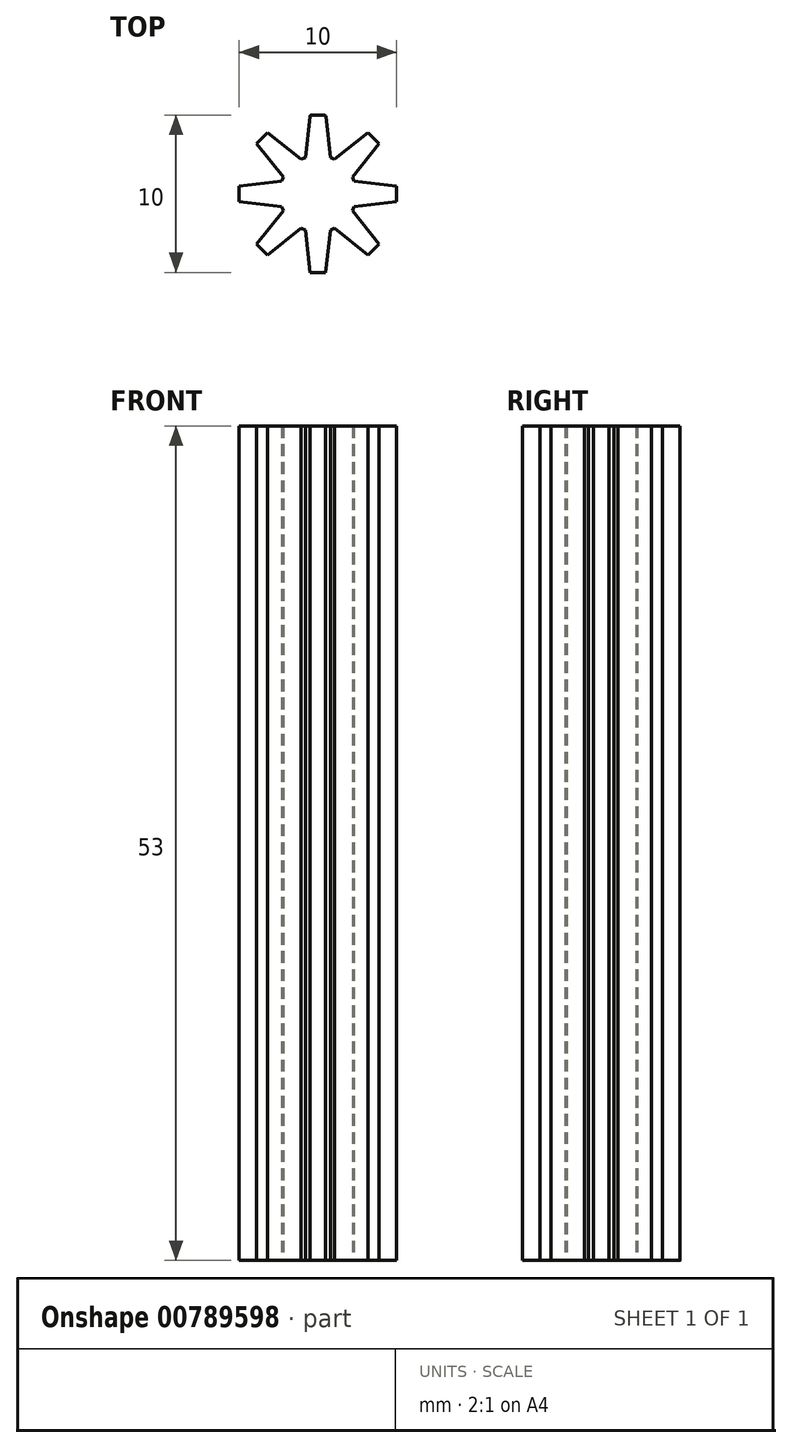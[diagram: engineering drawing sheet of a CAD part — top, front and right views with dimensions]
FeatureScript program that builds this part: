
annotation { "Feature Type Name" : "Feature", "Feature Type Description" : "" }
export const myFeature = defineFeature(function(context is Context, id is Id, definition is map)
    precondition{}
    {
        {
            var Q0;
            Q0=qCreatedBy(makeId("Top.planeOp"),FACE);
            var sketch = newSketch(context, id + "F0", { "sketchPlane" : qUnion([Q0])});
            skLineSegment(sketch, "E0", {"start": v(0, 5) * mm, "end": v(0.5, 5) * mm});
            skLineSegment(sketch, "E1", {"start": v(0.5, 5) * mm, "end": v(0.8, 2.3) * mm});
            skLineSegment(sketch, "E2.MirrorCS", {"start": v(-0.5, 5) * mm, "end": v(-0.8, 2.3) * mm});
            skLineSegment(sketch, "E3.MirrorCS", {"start": v(0, 5) * mm, "end": v(-0.5, 5) * mm});
            skLineSegment(sketch, "E4.1.0", {"start": v(-3.18, 3.89) * mm, "end": v(-1.06, 2.2) * mm});
            skLineSegment(sketch, "E4.1.1", {"start": v(-3.89, 3.18) * mm, "end": v(-2.2, 1.06) * mm});
            skLineSegment(sketch, "E4.1.2", {"start": v(-3.54, 3.54) * mm, "end": v(-3.89, 3.18) * mm});
            skLineSegment(sketch, "E4.1.3", {"start": v(-3.54, 3.54) * mm, "end": v(-3.18, 3.89) * mm});
            skLineSegment(sketch, "E4.1.4", {"start": v(-3.18, 3.89) * mm, "end": v(-1.06, 2.2) * mm});
            skLineSegment(sketch, "E4.1.5", {"start": v(-3.89, 3.18) * mm, "end": v(-2.2, 1.06) * mm});
            skLineSegment(sketch, "E4.1.6", {"start": v(-3.54, 3.54) * mm, "end": v(-3.18, 3.89) * mm});
            skLineSegment(sketch, "E4.1.7", {"start": v(-3.54, 3.54) * mm, "end": v(-3.89, 3.18) * mm});
            skLineSegment(sketch, "E4.1.8", {"start": v(-3.54, 3.54) * mm, "end": v(-3.89, 3.18) * mm});
            skLineSegment(sketch, "E4.1.9", {"start": v(-3.89, 3.18) * mm, "end": v(-2.2, 1.06) * mm});
            skLineSegment(sketch, "E4.1.10", {"start": v(-3.54, 3.54) * mm, "end": v(-3.18, 3.89) * mm});
            skLineSegment(sketch, "E4.1.11", {"start": v(-3.18, 3.89) * mm, "end": v(-1.06, 2.2) * mm});
            skLineSegment(sketch, "E4.1.12", {"start": v(-3.54, 3.54) * mm, "end": v(-3.89, 3.18) * mm});
            skLineSegment(sketch, "E4.1.13", {"start": v(-3.54, 3.54) * mm, "end": v(-3.18, 3.89) * mm});
            skLineSegment(sketch, "E4.2.0", {"start": v(-5, 0.5) * mm, "end": v(-2.3, 0.8) * mm});
            skLineSegment(sketch, "E4.2.1", {"start": v(-5, -0.5) * mm, "end": v(-2.3, -0.8) * mm});
            skLineSegment(sketch, "E4.2.2", {"start": v(-5, 0) * mm, "end": v(-5, -0.5) * mm});
            skLineSegment(sketch, "E4.2.3", {"start": v(-5, 0) * mm, "end": v(-5, 0.5) * mm});
            skLineSegment(sketch, "E4.2.4", {"start": v(-5, 0.5) * mm, "end": v(-2.3, 0.8) * mm});
            skLineSegment(sketch, "E4.2.5", {"start": v(-5, -0.5) * mm, "end": v(-2.3, -0.8) * mm});
            skLineSegment(sketch, "E4.2.6", {"start": v(-5, 0) * mm, "end": v(-5, 0.5) * mm});
            skLineSegment(sketch, "E4.2.7", {"start": v(-5, 0) * mm, "end": v(-5, -0.5) * mm});
            skLineSegment(sketch, "E4.2.8", {"start": v(-5, 0) * mm, "end": v(-5, -0.5) * mm});
            skLineSegment(sketch, "E4.2.9", {"start": v(-5, -0.5) * mm, "end": v(-2.3, -0.8) * mm});
            skLineSegment(sketch, "E4.2.10", {"start": v(-5, 0) * mm, "end": v(-5, 0.5) * mm});
            skLineSegment(sketch, "E4.2.11", {"start": v(-5, 0.5) * mm, "end": v(-2.3, 0.8) * mm});
            skLineSegment(sketch, "E4.2.12", {"start": v(-5, 0) * mm, "end": v(-5, -0.5) * mm});
            skLineSegment(sketch, "E4.2.13", {"start": v(-5, 0) * mm, "end": v(-5, 0.5) * mm});
            skLineSegment(sketch, "E4.3.0", {"start": v(-3.89, -3.18) * mm, "end": v(-2.2, -1.06) * mm});
            skLineSegment(sketch, "E4.3.1", {"start": v(-3.18, -3.89) * mm, "end": v(-1.06, -2.2) * mm});
            skLineSegment(sketch, "E4.3.2", {"start": v(-3.54, -3.54) * mm, "end": v(-3.18, -3.89) * mm});
            skLineSegment(sketch, "E4.3.3", {"start": v(-3.54, -3.54) * mm, "end": v(-3.89, -3.18) * mm});
            skLineSegment(sketch, "E4.3.4", {"start": v(-3.89, -3.18) * mm, "end": v(-2.2, -1.06) * mm});
            skLineSegment(sketch, "E4.3.5", {"start": v(-3.18, -3.89) * mm, "end": v(-1.06, -2.2) * mm});
            skLineSegment(sketch, "E4.3.6", {"start": v(-3.54, -3.54) * mm, "end": v(-3.89, -3.18) * mm});
            skLineSegment(sketch, "E4.3.7", {"start": v(-3.54, -3.54) * mm, "end": v(-3.18, -3.89) * mm});
            skLineSegment(sketch, "E4.3.8", {"start": v(-3.54, -3.54) * mm, "end": v(-3.18, -3.89) * mm});
            skLineSegment(sketch, "E4.3.9", {"start": v(-3.18, -3.89) * mm, "end": v(-1.06, -2.2) * mm});
            skLineSegment(sketch, "E4.3.10", {"start": v(-3.54, -3.54) * mm, "end": v(-3.89, -3.18) * mm});
            skLineSegment(sketch, "E4.3.11", {"start": v(-3.89, -3.18) * mm, "end": v(-2.2, -1.06) * mm});
            skLineSegment(sketch, "E4.3.12", {"start": v(-3.54, -3.54) * mm, "end": v(-3.18, -3.89) * mm});
            skLineSegment(sketch, "E4.3.13", {"start": v(-3.54, -3.54) * mm, "end": v(-3.89, -3.18) * mm});
            skLineSegment(sketch, "E4.4.0", {"start": v(-0.5, -5) * mm, "end": v(-0.8, -2.3) * mm});
            skLineSegment(sketch, "E4.4.1", {"start": v(0.5, -5) * mm, "end": v(0.8, -2.3) * mm});
            skLineSegment(sketch, "E4.4.2", {"start": v(0, -5) * mm, "end": v(0.5, -5) * mm});
            skLineSegment(sketch, "E4.4.3", {"start": v(0, -5) * mm, "end": v(-0.5, -5) * mm});
            skLineSegment(sketch, "E4.4.4", {"start": v(-0.5, -5) * mm, "end": v(-0.8, -2.3) * mm});
            skLineSegment(sketch, "E4.4.5", {"start": v(0.5, -5) * mm, "end": v(0.8, -2.3) * mm});
            skLineSegment(sketch, "E4.4.6", {"start": v(0, -5) * mm, "end": v(-0.5, -5) * mm});
            skLineSegment(sketch, "E4.4.7", {"start": v(0, -5) * mm, "end": v(0.5, -5) * mm});
            skLineSegment(sketch, "E4.4.8", {"start": v(0, -5) * mm, "end": v(0.5, -5) * mm});
            skLineSegment(sketch, "E4.4.9", {"start": v(0.5, -5) * mm, "end": v(0.8, -2.3) * mm});
            skLineSegment(sketch, "E4.4.10", {"start": v(0, -5) * mm, "end": v(-0.5, -5) * mm});
            skLineSegment(sketch, "E4.4.11", {"start": v(-0.5, -5) * mm, "end": v(-0.8, -2.3) * mm});
            skLineSegment(sketch, "E4.4.12", {"start": v(0, -5) * mm, "end": v(0.5, -5) * mm});
            skLineSegment(sketch, "E4.4.13", {"start": v(0, -5) * mm, "end": v(-0.5, -5) * mm});
            skLineSegment(sketch, "E4.5.0", {"start": v(3.18, -3.89) * mm, "end": v(1.06, -2.2) * mm});
            skLineSegment(sketch, "E4.5.1", {"start": v(3.89, -3.18) * mm, "end": v(2.2, -1.06) * mm});
            skLineSegment(sketch, "E4.5.2", {"start": v(3.54, -3.54) * mm, "end": v(3.89, -3.18) * mm});
            skLineSegment(sketch, "E4.5.3", {"start": v(3.54, -3.54) * mm, "end": v(3.18, -3.89) * mm});
            skLineSegment(sketch, "E4.5.4", {"start": v(3.18, -3.89) * mm, "end": v(1.06, -2.2) * mm});
            skLineSegment(sketch, "E4.5.5", {"start": v(3.89, -3.18) * mm, "end": v(2.2, -1.06) * mm});
            skLineSegment(sketch, "E4.5.6", {"start": v(3.54, -3.54) * mm, "end": v(3.18, -3.89) * mm});
            skLineSegment(sketch, "E4.5.7", {"start": v(3.54, -3.54) * mm, "end": v(3.89, -3.18) * mm});
            skLineSegment(sketch, "E4.5.8", {"start": v(3.54, -3.54) * mm, "end": v(3.89, -3.18) * mm});
            skLineSegment(sketch, "E4.5.9", {"start": v(3.89, -3.18) * mm, "end": v(2.2, -1.06) * mm});
            skLineSegment(sketch, "E4.5.10", {"start": v(3.54, -3.54) * mm, "end": v(3.18, -3.89) * mm});
            skLineSegment(sketch, "E4.5.11", {"start": v(3.18, -3.89) * mm, "end": v(1.06, -2.2) * mm});
            skLineSegment(sketch, "E4.5.12", {"start": v(3.54, -3.54) * mm, "end": v(3.89, -3.18) * mm});
            skLineSegment(sketch, "E4.5.13", {"start": v(3.54, -3.54) * mm, "end": v(3.18, -3.89) * mm});
            skLineSegment(sketch, "E4.6.0", {"start": v(5, -0.5) * mm, "end": v(2.3, -0.8) * mm});
            skLineSegment(sketch, "E4.6.1", {"start": v(5, 0.5) * mm, "end": v(2.3, 0.8) * mm});
            skLineSegment(sketch, "E4.6.2", {"start": v(5, 0) * mm, "end": v(5, 0.5) * mm});
            skLineSegment(sketch, "E4.6.3", {"start": v(5, 0) * mm, "end": v(5, -0.5) * mm});
            skLineSegment(sketch, "E4.6.4", {"start": v(5, -0.5) * mm, "end": v(2.3, -0.8) * mm});
            skLineSegment(sketch, "E4.6.5", {"start": v(5, 0.5) * mm, "end": v(2.3, 0.8) * mm});
            skLineSegment(sketch, "E4.6.6", {"start": v(5, 0) * mm, "end": v(5, -0.5) * mm});
            skLineSegment(sketch, "E4.6.7", {"start": v(5, 0) * mm, "end": v(5, 0.5) * mm});
            skLineSegment(sketch, "E4.6.8", {"start": v(5, 0) * mm, "end": v(5, 0.5) * mm});
            skLineSegment(sketch, "E4.6.9", {"start": v(5, 0.5) * mm, "end": v(2.3, 0.8) * mm});
            skLineSegment(sketch, "E4.6.10", {"start": v(5, 0) * mm, "end": v(5, -0.5) * mm});
            skLineSegment(sketch, "E4.6.11", {"start": v(5, -0.5) * mm, "end": v(2.3, -0.8) * mm});
            skLineSegment(sketch, "E4.6.12", {"start": v(5, 0) * mm, "end": v(5, 0.5) * mm});
            skLineSegment(sketch, "E4.6.13", {"start": v(5, 0) * mm, "end": v(5, -0.5) * mm});
            skLineSegment(sketch, "E4.7.0", {"start": v(3.89, 3.18) * mm, "end": v(2.2, 1.06) * mm});
            skLineSegment(sketch, "E4.7.1", {"start": v(3.18, 3.89) * mm, "end": v(1.06, 2.2) * mm});
            skLineSegment(sketch, "E4.7.2", {"start": v(3.54, 3.54) * mm, "end": v(3.18, 3.89) * mm});
            skLineSegment(sketch, "E4.7.3", {"start": v(3.54, 3.54) * mm, "end": v(3.89, 3.18) * mm});
            skLineSegment(sketch, "E4.7.4", {"start": v(3.89, 3.18) * mm, "end": v(2.2, 1.06) * mm});
            skLineSegment(sketch, "E4.7.5", {"start": v(3.18, 3.89) * mm, "end": v(1.06, 2.2) * mm});
            skLineSegment(sketch, "E4.7.6", {"start": v(3.54, 3.54) * mm, "end": v(3.89, 3.18) * mm});
            skLineSegment(sketch, "E4.7.7", {"start": v(3.54, 3.54) * mm, "end": v(3.18, 3.89) * mm});
            skLineSegment(sketch, "E4.7.8", {"start": v(3.54, 3.54) * mm, "end": v(3.18, 3.89) * mm});
            skLineSegment(sketch, "E4.7.9", {"start": v(3.18, 3.89) * mm, "end": v(1.06, 2.2) * mm});
            skLineSegment(sketch, "E4.7.10", {"start": v(3.54, 3.54) * mm, "end": v(3.89, 3.18) * mm});
            skLineSegment(sketch, "E4.7.11", {"start": v(3.89, 3.18) * mm, "end": v(2.2, 1.06) * mm});
            skLineSegment(sketch, "E4.7.12", {"start": v(3.54, 3.54) * mm, "end": v(3.18, 3.89) * mm});
            skLineSegment(sketch, "E4.7.13", {"start": v(3.54, 3.54) * mm, "end": v(3.89, 3.18) * mm});
            skPoint(sketch, "E4.center", {"position": v(0, 0) * mm});
            skLineSegment(sketch, "E5", {"start": v(-2.2, 1.06) * mm, "end": v(-2.3, 0.8) * mm});
            skLineSegment(sketch, "E6", {"start": v(-2.3, -0.8) * mm, "end": v(-2.2, -1.06) * mm});
            skLineSegment(sketch, "E7", {"start": v(-1.06, -2.2) * mm, "end": v(-0.8, -2.3) * mm});
            skLineSegment(sketch, "E8", {"start": v(0.8, -2.3) * mm, "end": v(1.06, -2.2) * mm});
            skLineSegment(sketch, "E9", {"start": v(2.2, -1.06) * mm, "end": v(2.3, -0.8) * mm});
            skLineSegment(sketch, "E10", {"start": v(2.3, 0.8) * mm, "end": v(2.2, 1.06) * mm});
            skLineSegment(sketch, "E11", {"start": v(1.06, 2.2) * mm, "end": v(0.8, 2.3) * mm});
            skLineSegment(sketch, "E12", {"start": v(-0.8, 2.3) * mm, "end": v(-1.06, 2.2) * mm});
            skSolve(sketch);
        }
        {
            var Q0;
            Q0 = qSketchRegion(id + "F0", true);
            extrude(context, id + "F1", {"entities" : qUnion([Q0]), "depth" : 53 * mm, "offsetDistance" : 25 * mm});
        }
        {
            var Q0;
            Q0=makeQuery(id+"F1.opExtrude","SWEPT_EDGE",EDGE,{"disambiguationData":[OSD([sQuery(id+"F0.wireOp",EDGE,"E4.7.11"),sQuery(id+"F0.wireOp",EDGE,"E4.7.13")])]});
            var Q1;
            Q1=makeQuery(id+"F1.opExtrude","SWEPT_EDGE",EDGE,{"disambiguationData":[OSD([sQuery(id+"F0.wireOp",EDGE,"E4.7.9"),sQuery(id+"F0.wireOp",EDGE,"E4.7.12")])]});
            var Q2;
            Q2=makeQuery(id+"F1.opExtrude","SWEPT_EDGE",EDGE,{"disambiguationData":[OSD([sQuery(id+"F0.wireOp",EDGE,"E4.6.9"),sQuery(id+"F0.wireOp",EDGE,"E4.6.12")])]});
            var Q3;
            Q3=makeQuery(id+"F1.opExtrude","SWEPT_EDGE",EDGE,{"disambiguationData":[OSD([sQuery(id+"F0.wireOp",EDGE,"E4.6.11"),sQuery(id+"F0.wireOp",EDGE,"E4.6.13")])]});
            var Q4;
            Q4=makeQuery(id+"F1.opExtrude","SWEPT_EDGE",EDGE,{"disambiguationData":[OSD([sQuery(id+"F0.wireOp",EDGE,"E4.5.9"),sQuery(id+"F0.wireOp",EDGE,"E4.5.12")])]});
            var Q5;
            Q5=makeQuery(id+"F1.opExtrude","SWEPT_EDGE",EDGE,{"disambiguationData":[OSD([sQuery(id+"F0.wireOp",EDGE,"E4.5.11"),sQuery(id+"F0.wireOp",EDGE,"E4.5.13")])]});
            var Q6;
            Q6=makeQuery(id+"F1.opExtrude","SWEPT_EDGE",EDGE,{"disambiguationData":[OSD([sQuery(id+"F0.wireOp",EDGE,"E4.3.11"),sQuery(id+"F0.wireOp",EDGE,"E4.3.13")])]});
            var Q7;
            Q7=makeQuery(id+"F1.opExtrude","SWEPT_EDGE",EDGE,{"disambiguationData":[OSD([sQuery(id+"F0.wireOp",EDGE,"E4.3.9"),sQuery(id+"F0.wireOp",EDGE,"E4.3.12")])]});
            var Q8;
            Q8=makeQuery(id+"F1.opExtrude","SWEPT_EDGE",EDGE,{"disambiguationData":[OSD([sQuery(id+"F0.wireOp",EDGE,"E4.4.11"),sQuery(id+"F0.wireOp",EDGE,"E4.4.13")])]});
            var Q9;
            Q9=makeQuery(id+"F1.opExtrude","SWEPT_EDGE",EDGE,{"disambiguationData":[OSD([sQuery(id+"F0.wireOp",EDGE,"E4.4.9"),sQuery(id+"F0.wireOp",EDGE,"E4.4.12")])]});
            var Q10;
            Q10=makeQuery(id+"F1.opExtrude","SWEPT_EDGE",EDGE,{"disambiguationData":[OSD([sQuery(id+"F0.wireOp",EDGE,"E4.2.9"),sQuery(id+"F0.wireOp",EDGE,"E4.2.12")])]});
            var Q11;
            Q11=makeQuery(id+"F1.opExtrude","SWEPT_EDGE",EDGE,{"disambiguationData":[OSD([sQuery(id+"F0.wireOp",EDGE,"E4.2.11"),sQuery(id+"F0.wireOp",EDGE,"E4.2.13")])]});
            var Q12;
            Q12=makeQuery(id+"F1.opExtrude","SWEPT_EDGE",EDGE,{"disambiguationData":[OSD([sQuery(id+"F0.wireOp",EDGE,"E4.1.9"),sQuery(id+"F0.wireOp",EDGE,"E4.1.12")])]});
            var Q13;
            Q13=makeQuery(id+"F1.opExtrude","SWEPT_EDGE",EDGE,{"disambiguationData":[OSD([sQuery(id+"F0.wireOp",EDGE,"E4.1.11"),sQuery(id+"F0.wireOp",EDGE,"E4.1.13")])]});
            var Q14;
            Q14=makeQuery(id+"F1.opExtrude","SWEPT_EDGE",EDGE,{"disambiguationData":[OSD([sQuery(id+"F0.wireOp",EDGE,"E2.MirrorCS"),sQuery(id+"F0.wireOp",EDGE,"E3.MirrorCS")])]});
            var Q15;
            Q15=makeQuery(id+"F1.opExtrude","SWEPT_EDGE",EDGE,{"disambiguationData":[OSD([sQuery(id+"F0.wireOp",EDGE,"E1"),sQuery(id+"F0.wireOp",EDGE,"E0")])]});
            fillet(context, id + "F2", {"entities" : qUnion([Q0, Q1, Q2, Q3, Q4, Q5, Q6, Q7, Q8, Q9, Q10, Q11, Q12, Q13, Q14, Q15]), "radius" : .1 * mm, "tangentPropagation" : true, "allowEdgeOverflow" : false});
        }
        {
            var Q0;
            Q0=makeQuery(id+"F1.opExtrude","CAP_FACE",FACE,{"disambiguationData":[OSD([sQuery(id+"F0.wireOp",EDGE,"E1"),sQuery(id+"F0.wireOp",EDGE,"E2.MirrorCS"),sQuery(id+"F0.wireOp",EDGE,"E3.MirrorCS"),sQuery(id+"F0.wireOp",EDGE,"E0"),sQuery(id+"F0.wireOp",EDGE,"E4.1.9"),sQuery(id+"F0.wireOp",EDGE,"E4.1.11"),sQuery(id+"F0.wireOp",EDGE,"E4.1.12"),sQuery(id+"F0.wireOp",EDGE,"E4.1.13"),sQuery(id+"F0.wireOp",EDGE,"E4.2.9"),sQuery(id+"F0.wireOp",EDGE,"E4.2.11"),sQuery(id+"F0.wireOp",EDGE,"E4.2.12"),sQuery(id+"F0.wireOp",EDGE,"E4.2.13"),sQuery(id+"F0.wireOp",EDGE,"E4.3.9"),sQuery(id+"F0.wireOp",EDGE,"E4.3.11"),sQuery(id+"F0.wireOp",EDGE,"E4.3.12"),sQuery(id+"F0.wireOp",EDGE,"E4.3.13"),sQuery(id+"F0.wireOp",EDGE,"E4.4.9"),sQuery(id+"F0.wireOp",EDGE,"E4.4.11"),sQuery(id+"F0.wireOp",EDGE,"E4.4.12"),sQuery(id+"F0.wireOp",EDGE,"E4.4.13"),sQuery(id+"F0.wireOp",EDGE,"E4.5.9"),sQuery(id+"F0.wireOp",EDGE,"E4.5.11"),sQuery(id+"F0.wireOp",EDGE,"E4.5.12"),sQuery(id+"F0.wireOp",EDGE,"E4.5.13"),sQuery(id+"F0.wireOp",EDGE,"E4.6.9"),sQuery(id+"F0.wireOp",EDGE,"E4.6.11"),sQuery(id+"F0.wireOp",EDGE,"E4.6.12"),sQuery(id+"F0.wireOp",EDGE,"E4.6.13"),sQuery(id+"F0.wireOp",EDGE,"E4.7.9"),sQuery(id+"F0.wireOp",EDGE,"E4.7.11"),sQuery(id+"F0.wireOp",EDGE,"E4.7.12"),sQuery(id+"F0.wireOp",EDGE,"E4.7.13"),sQuery(id+"F0.wireOp",EDGE,"E5"),sQuery(id+"F0.wireOp",EDGE,"E6"),sQuery(id+"F0.wireOp",EDGE,"E7"),sQuery(id+"F0.wireOp",EDGE,"E8"),sQuery(id+"F0.wireOp",EDGE,"E9"),sQuery(id+"F0.wireOp",EDGE,"E10"),sQuery(id+"F0.wireOp",EDGE,"E11"),sQuery(id+"F0.wireOp",EDGE,"E12")])],"isStart":true});
            var sketch = newSketch(context, id + "F3", { "sketchPlane" : qUnion([Q0])});
            skCircle(sketch, "E13", {"center": v(0, 0) * mm, "radius": 1.4 * mm});
            skSolve(sketch);
        }
        {
            var Q0;
            Q0 = qSketchRegion(id + "F3", true);
            extrude(context, id + "F4", {"entities" : qUnion([Q0]), "depth" : 10 * mm, "offsetDistance" : 25 * mm});
        }
        {
            var Q0;
            Q0=makeQuery(id+"F4.opExtrude","SWEPT_BODY",BODY,{"disambiguationData":[OSD([sQuery(id+"F3.wireOp",EDGE,"E13")])]});
            deleteBodies(context, id + "F5", {"entities" : qUnion([Q0])});
        }
    });
